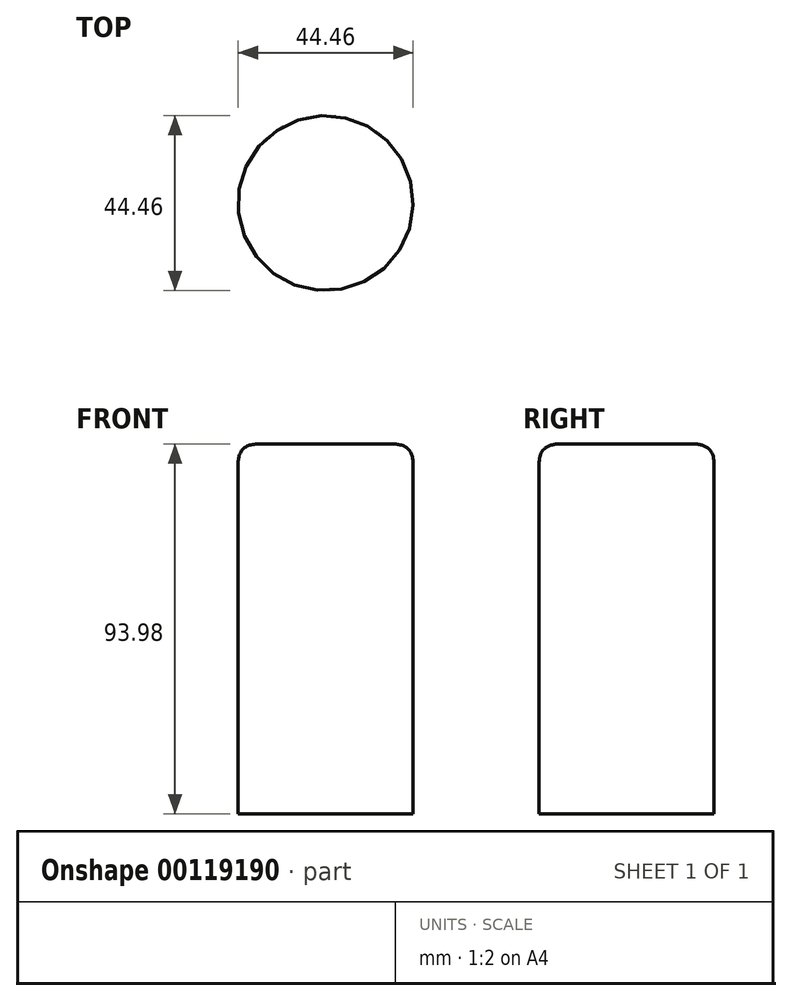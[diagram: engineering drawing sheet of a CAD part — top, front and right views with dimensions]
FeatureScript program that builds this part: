
annotation { "Feature Type Name" : "Feature", "Feature Type Description" : "" }
export const myFeature = defineFeature(function(context is Context, id is Id, definition is map)
    precondition{}
    {
        {
            var Q0;
            Q0=qCreatedBy(makeId("Top.planeOp"),FACE);
            var sketch = newSketch(context, id + "F0", { "sketchPlane" : qUnion([Q0])});
            skCircle(sketch, "E0", {"center": v(0, 0) * mm, "radius": 22.23 * mm});
            skSolve(sketch);
        }
        {
            var Q0;
            Q0 = qSketchRegion(id + "F0", true);
            extrude(context, id + "F1", {"entities" : qUnion([Q0]), "depth" : 93.98 * mm});
        }
        {
            var Q0;
            Q0=makeQuery(id+"F1.opExtrude","CAP_EDGE",EDGE,{"disambiguationData":[OSD([sQuery(id+"F0.wireOp",EDGE,"E0")])],"isStart":false});
            fillet(context, id + "F2", {"entities" : qUnion([Q0]), "radius" : 5.08 * mm, "tangentPropagation" : true, "rho" : 0.5, "crossSection" : FilletCrossSection.CONIC, "allowEdgeOverflow" : false});
        }
        {
            var Q0;
            Q0=makeQuery(id+"F1.opExtrude","SWEPT_BODY",BODY,{"disambiguationData":[OSD([sQuery(id+"F0.wireOp",EDGE,"E0")])]});
            var Q1;
            Q1=makeQuery(id+"F1.opExtrude","CAP_EDGE",EDGE,{"disambiguationData":[OSD([sQuery(id+"F0.wireOp",EDGE,"E0")])],"isStart":true});
            transform(context, id + "F3", {"entities" : qUnion([Q0]), "transformType" : TransformType.ROTATION, "transformAxis" : qUnion([Q1]), "angle" : 30 * degree, "makeCopy" : false});
        }
    });
